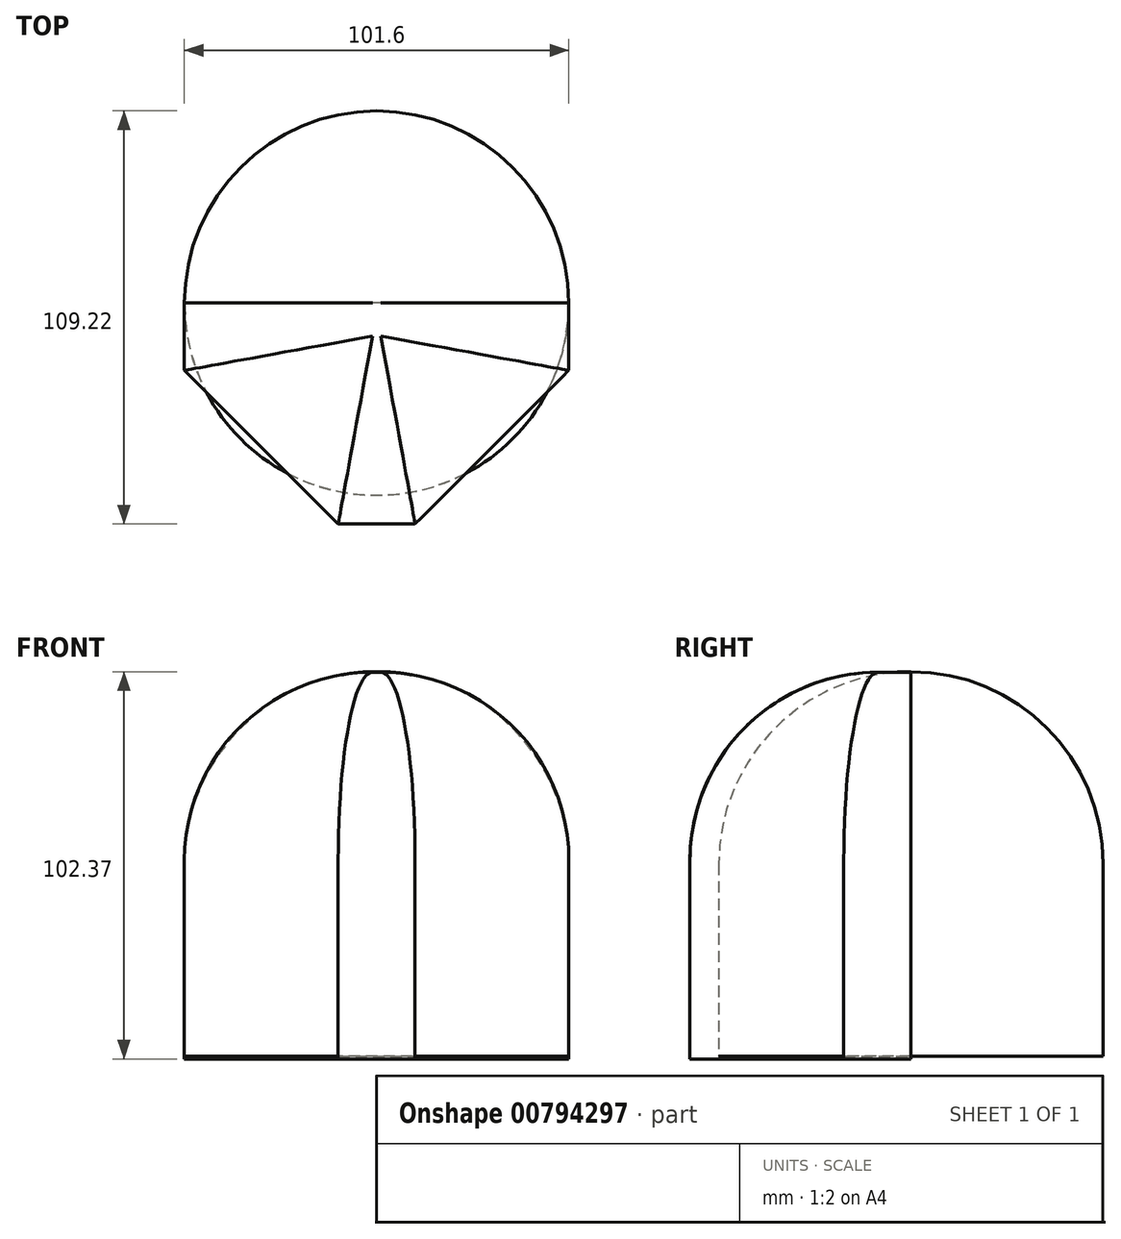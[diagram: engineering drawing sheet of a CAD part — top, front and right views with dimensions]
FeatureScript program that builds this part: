
annotation { "Feature Type Name" : "Feature", "Feature Type Description" : "" }
export const myFeature = defineFeature(function(context is Context, id is Id, definition is map)
    precondition{}
    {
        {
            var Q0;
            Q0=qCreatedBy(makeId("Top.planeOp"),FACE);
            var sketch = newSketch(context, id + "F0", { "sketchPlane" : qUnion([Q0])});
            skCircle(sketch, "E0", {"center": v(0, 0) * mm, "radius": 50.8 * mm});
            skSolve(sketch);
        }
        {
            var Q0;
            Q0 = qSketchRegion(id + "F0", true);
            extrude(context, id + "F1", {"entities" : qUnion([Q0]), "endBound" : BoundingType.SYMMETRIC, "depth" : 101.6 * mm, "offsetDistance" : 25.4 * mm});
        }
        {
            var Q0;
            Q0=makeQuery(id+"F1.opExtrude","CAP_EDGE",EDGE,{"disambiguationData":[OSD([sQuery(id+"F0.wireOp",EDGE,"E0")])],"isStart":false});
            fillet(context, id + "F2", {"entities" : qUnion([Q0]), "radius" : 50.8 * mm, "tangentPropagation" : true, "allowEdgeOverflow" : false});
        }
        {
            var Q0;
            Q0=qCreatedBy(makeId("Right.planeOp"),FACE);
            var sketch = newSketch(context, id + "F3", { "sketchPlane" : qUnion([Q0])});
            skLineSegment(sketch, "E1.bottom", {"start": v(0, 50.62) * mm, "end": v(-58.42, 50.62) * mm});
            skLineSegment(sketch, "E1.top", {"start": v(0, -51.57) * mm, "end": v(-58.42, -51.57) * mm});
            skLineSegment(sketch, "E1.left", {"start": v(0, 50.62) * mm, "end": v(0, -51.57) * mm});
            skLineSegment(sketch, "E1.right", {"start": v(-58.42, 50.62) * mm, "end": v(-58.42, -51.57) * mm});
            skSolve(sketch);
        }
        {
            var Q0;
            Q0 = qSketchRegion(id + "F3", true);
            extrude(context, id + "F4", {"entities" : qUnion([Q0]), "endBound" : BoundingType.SYMMETRIC, "depth" : 101.6 * mm, "offsetDistance" : 25.4 * mm});
        }
        {
            var Q0;
            Q0=makeQuery(id+"F4.opExtrude","SWEPT_EDGE",EDGE,{"disambiguationData":[OSD([sQuery(id+"F3.wireOp",EDGE,"E1.bottom"),sQuery(id+"F3.wireOp",EDGE,"E1.right")])]});
            var Q1;
            Q1=makeQuery(id+"F4.opExtrude","CAP_EDGE",EDGE,{"disambiguationData":[OSD([sQuery(id+"F3.wireOp",EDGE,"E1.bottom")])],"isStart":false});
            var Q2;
            Q2=makeQuery(id+"F4.opExtrude","CAP_EDGE",EDGE,{"disambiguationData":[OSD([sQuery(id+"F3.wireOp",EDGE,"E1.bottom")])],"isStart":true});
            fillet(context, id + "F5", {"entities" : qUnion([Q0, Q1, Q2]), "radius" : 49.67 * mm, "tangentPropagation" : true, "allowEdgeOverflow" : false});
        }
        {
            var Q0;
            Q0=makeQuery(id+"F4.opExtrude","CAP_EDGE",EDGE,{"disambiguationData":[OSD([sQuery(id+"F3.wireOp",EDGE,"E1.right")])],"isStart":true});
            var Q1;
            Q1=makeQuery(id+"F4.opExtrude","CAP_EDGE",EDGE,{"disambiguationData":[OSD([sQuery(id+"F3.wireOp",EDGE,"E1.right")])],"isStart":false});
            chamfer(context, id + "F6", {"entities" : qUnion([Q0, Q1]), "width" : 40.64 * mm, "tangentPropagation" : true});
        }
    });
